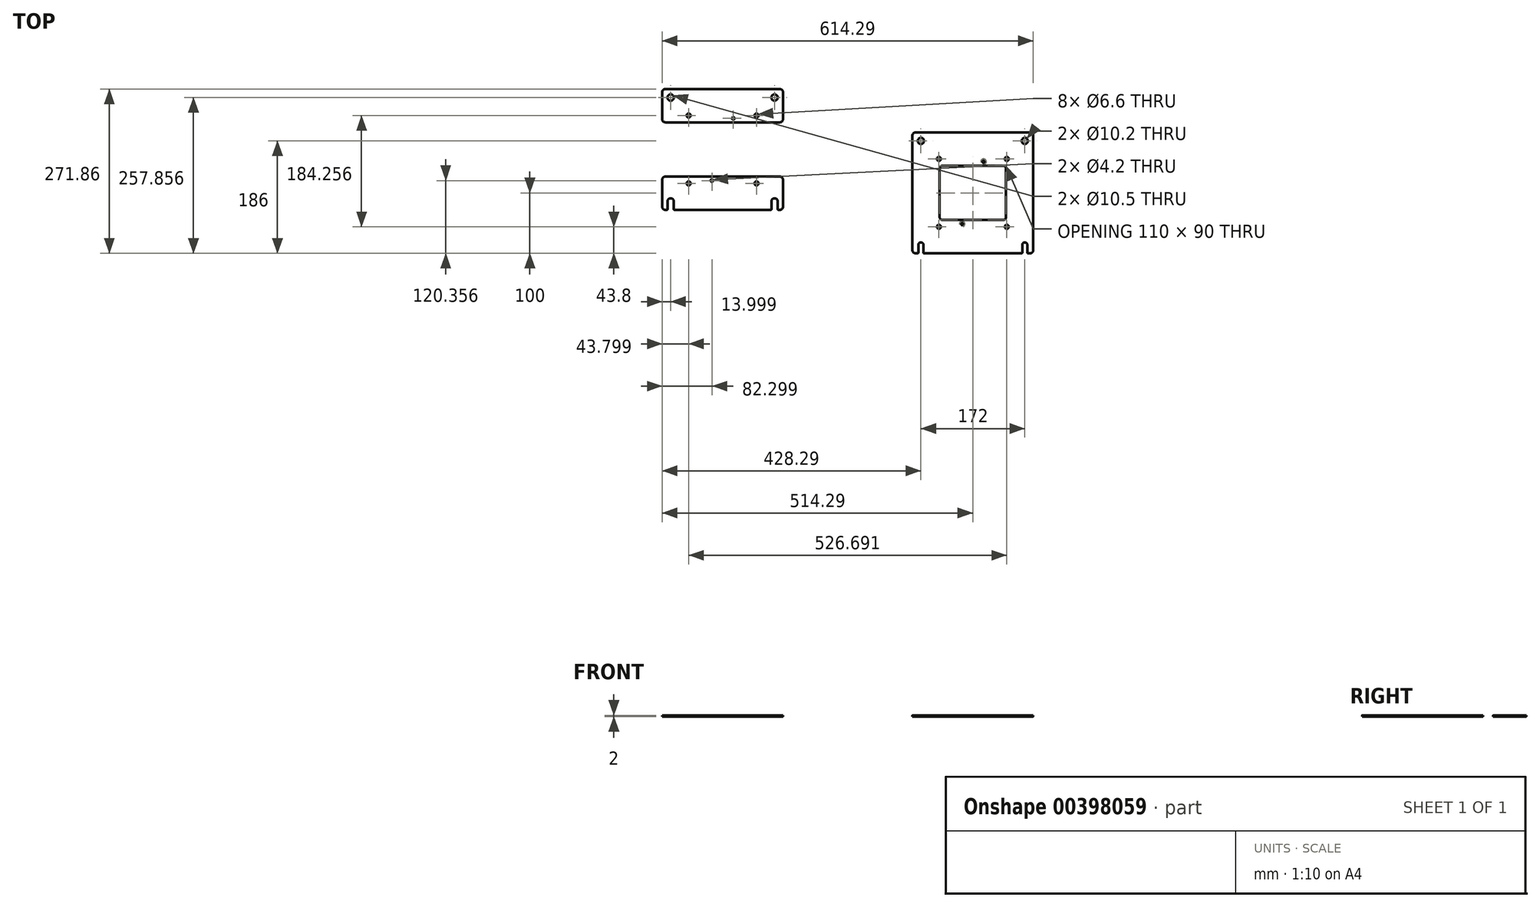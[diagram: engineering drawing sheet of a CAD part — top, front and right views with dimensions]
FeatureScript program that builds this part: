
annotation { "Feature Type Name" : "Feature", "Feature Type Description" : "" }
export const myFeature = defineFeature(function(context is Context, id is Id, definition is map)
    precondition{}
    {
        {
            var Q0;
            Q0=qCreatedBy(makeId("Top.planeOp"),FACE);
            var sketch = newSketch(context, id + "F0", { "sketchPlane" : qUnion([Q0])});
            skLineSegment(sketch, "E0.bottom", {"start": v(-95, -100) * mm, "end": v(-91.1, -100) * mm});
            skLineSegment(sketch, "E0.top", {"start": v(-95, 100) * mm, "end": v(95, 100) * mm});
            skLineSegment(sketch, "E0.left", {"start": v(-100, -95) * mm, "end": v(-100, 95) * mm});
            skLineSegment(sketch, "E0.right", {"start": v(100, -95) * mm, "end": v(100, 95) * mm});
            skPoint(sketch, "E0.middle", {"position": v(0, 0) * mm});
            skLineSegment(sketch, "E1.bottom", {"start": v(-50, -45) * mm, "end": v(50, -45) * mm});
            skLineSegment(sketch, "E1.top", {"start": v(-50, 45) * mm, "end": v(50, 45) * mm});
            skLineSegment(sketch, "E1.left", {"start": v(-55, -40) * mm, "end": v(-55, 40) * mm});
            skLineSegment(sketch, "E1.right", {"start": v(55, -40) * mm, "end": v(55, 40) * mm});
            skLineSegment(sketch, "E2", {"start": v(0, 119.48) * mm, "end": v(0, -138.55) * mm, "construction": true});
            skPoint(sketch, "E2.endSnap0", {"position": v(0, -45) * mm});
            skLineSegment(sketch, "E3", {"start": v(138.1, 0) * mm, "end": v(-145.7, 0) * mm, "construction": true});
            skPoint(sketch, "E4.visualSharp", {"position": v(-100, 100) * mm});
            skArc(sketch, "E4.filletArc", {"start": v(-95, 100) * mm, "mid": v(-98.54, 98.54) * mm, "end": v(-100, 95) * mm});
            skPoint(sketch, "E5.visualSharp", {"position": v(-100, -100) * mm});
            skArc(sketch, "E5.filletArc", {"start": v(-100, -95) * mm, "mid": v(-98.54, -98.54) * mm, "end": v(-95, -100) * mm});
            skPoint(sketch, "E6.visualSharp", {"position": v(100, -100) * mm});
            skArc(sketch, "E6.filletArc", {"start": v(95, -100) * mm, "mid": v(98.54, -98.54) * mm, "end": v(100, -95) * mm});
            skPoint(sketch, "E7.visualSharp", {"position": v(100, 100) * mm});
            skArc(sketch, "E7.filletArc", {"start": v(100, 95) * mm, "mid": v(98.54, 98.54) * mm, "end": v(95, 100) * mm});
            skPoint(sketch, "E8.visualSharp", {"position": v(-55, 45) * mm});
            skArc(sketch, "E8.filletArc", {"start": v(-50, 45) * mm, "mid": v(-53.54, 43.54) * mm, "end": v(-55, 40) * mm});
            skPoint(sketch, "E9.visualSharp", {"position": v(55, 45) * mm});
            skArc(sketch, "E9.filletArc", {"start": v(55, 40) * mm, "mid": v(53.54, 43.54) * mm, "end": v(50, 45) * mm});
            skPoint(sketch, "E10.visualSharp", {"position": v(55, -45) * mm});
            skArc(sketch, "E10.filletArc", {"start": v(50, -45) * mm, "mid": v(53.54, -43.54) * mm, "end": v(55, -40) * mm});
            skPoint(sketch, "E11.visualSharp", {"position": v(-55, -45) * mm});
            skArc(sketch, "E11.filletArc", {"start": v(-55, -40) * mm, "mid": v(-53.54, -43.54) * mm, "end": v(-50, -45) * mm});
            skCircle(sketch, "E12", {"center": v(-86, 86) * mm, "radius": 4.1 * mm});
            skCircle(sketch, "E13.MirrorC", {"center": v(86, 86) * mm, "radius": 4.1 * mm});
            skArc(sketch, "E14.MirrorC", {"start": v(-90.1, -86) * mm, "mid": v(-86, -81.9) * mm, "end": v(-81.9, -86) * mm});
            skArc(sketch, "E15.MirrorC", {"start": v(90.1, -86) * mm, "mid": v(86, -81.9) * mm, "end": v(81.9, -86) * mm});
            skPoint(sketch, "E16.centerSnap0", {"position": v(-53.54, 43.54) * mm});
            skCircle(sketch, "E17", {"center": v(-56.2, 56.2) * mm, "radius": 3.3 * mm});
            skCircle(sketch, "E18.MirrorC", {"center": v(56.2, 56.2) * mm, "radius": 3.3 * mm});
            skCircle(sketch, "E19.MirrorC", {"center": v(56.2, -56.2) * mm, "radius": 3.3 * mm});
            skCircle(sketch, "E20.MirrorC", {"center": v(-56.2, -56.2) * mm, "radius": 3.3 * mm});
            skCircle(sketch, "E21", {"center": v(17.7, 51.5) * mm, "radius": 1.55 * mm});
            skCircle(sketch, "E22", {"center": v(-17.7, -51.5) * mm, "radius": 1.55 * mm});
            skLineSegment(sketch, "E23", {"start": v(-81.9, -86) * mm, "end": v(-81.9, -99) * mm});
            skLineSegment(sketch, "E24", {"start": v(-90.1, -86) * mm, "end": v(-90.1, -99) * mm});
            skLineSegment(sketch, "E25.trimOffspring", {"start": v(-80.9, -100) * mm, "end": v(80.9, -100) * mm});
            skLineSegment(sketch, "E26.MirrorCS", {"start": v(81.9, -86) * mm, "end": v(81.9, -99) * mm});
            skLineSegment(sketch, "E27.MirrorCS", {"start": v(90.1, -86) * mm, "end": v(90.1, -99) * mm});
            skLineSegment(sketch, "E28.trimOffspring", {"start": v(91.1, -100) * mm, "end": v(95, -100) * mm});
            skPoint(sketch, "E29.visualSharp", {"position": v(-90.1, -100) * mm});
            skArc(sketch, "E29.filletArc", {"start": v(-91.1, -100) * mm, "mid": v(-90.4, -99.7) * mm, "end": v(-90.1, -99) * mm});
            skPoint(sketch, "E30.visualSharp", {"position": v(-81.9, -100) * mm});
            skArc(sketch, "E30.filletArc", {"start": v(-81.9, -99) * mm, "mid": v(-81.6, -99.7) * mm, "end": v(-80.9, -100) * mm});
            skPoint(sketch, "E31.visualSharp", {"position": v(90.1, -100) * mm});
            skArc(sketch, "E31.filletArc", {"start": v(90.1, -99) * mm, "mid": v(90.4, -99.7) * mm, "end": v(91.1, -100) * mm});
            skPoint(sketch, "E32.visualSharp", {"position": v(81.9, -100) * mm});
            skArc(sketch, "E32.filletArc", {"start": v(80.9, -100) * mm, "mid": v(81.6, -99.7) * mm, "end": v(81.9, -99) * mm});
            skLineSegment(sketch, "E33.bottom", {"start": v(-509.3, -28.14) * mm, "end": v(-506.54, -28.14) * mm});
            skLineSegment(sketch, "E33.top", {"start": v(-509.3, 171.86) * mm, "end": v(-319.3, 171.86) * mm});
            skLineSegment(sketch, "E33.left", {"start": v(-514.3, -23.14) * mm, "end": v(-514.3, 21.86) * mm});
            skLineSegment(sketch, "E33.right", {"start": v(-314.3, -23.14) * mm, "end": v(-314.3, 21.86) * mm});
            skPoint(sketch, "E33.middle", {"position": v(-414.3, 71.86) * mm});
            skLineSegment(sketch, "E34.bottom", {"start": v(-464.3, 26.86) * mm, "end": v(-364.3, 26.86) * mm});
            skLineSegment(sketch, "E34.top", {"start": v(-464.3, 116.86) * mm, "end": v(-364.3, 116.86) * mm});
            skLineSegment(sketch, "E35", {"start": v(-414.3, 191.33) * mm, "end": v(-414.3, -66.7) * mm, "construction": true});
            skPoint(sketch, "E35.endSnap0", {"position": v(-414.3, 26.86) * mm});
            skLineSegment(sketch, "E36", {"start": v(-276.2, 71.86) * mm, "end": v(-560, 71.86) * mm, "construction": true});
            skPoint(sketch, "E37.visualSharp", {"position": v(-514.3, 171.86) * mm});
            skArc(sketch, "E37.filletArc", {"start": v(-509.3, 171.86) * mm, "mid": v(-512.83, 170.4) * mm, "end": v(-514.3, 166.86) * mm});
            skPoint(sketch, "E38.visualSharp", {"position": v(-514.3, -28.14) * mm});
            skArc(sketch, "E38.filletArc", {"start": v(-514.3, -23.14) * mm, "mid": v(-512.83, -26.68) * mm, "end": v(-509.3, -28.14) * mm});
            skPoint(sketch, "E39.visualSharp", {"position": v(-314.3, -28.14) * mm});
            skArc(sketch, "E39.filletArc", {"start": v(-319.3, -28.14) * mm, "mid": v(-315.76, -26.68) * mm, "end": v(-314.3, -23.14) * mm});
            skPoint(sketch, "E40.visualSharp", {"position": v(-314.3, 171.86) * mm});
            skArc(sketch, "E40.filletArc", {"start": v(-314.3, 166.86) * mm, "mid": v(-315.76, 170.4) * mm, "end": v(-319.3, 171.86) * mm});
            skPoint(sketch, "E41.visualSharp", {"position": v(-359.3, 116.86) * mm});
            skPoint(sketch, "E42.visualSharp", {"position": v(-359.3, 26.86) * mm});
            skPoint(sketch, "E43.visualSharp", {"position": v(-469.3, 26.86) * mm});
            skCircle(sketch, "E44", {"center": v(-500.3, 157.86) * mm, "radius": 5.25 * mm});
            skCircle(sketch, "E45.MirrorC", {"center": v(-328.3, 157.86) * mm, "radius": 5.25 * mm});
            skArc(sketch, "E46.MirrorC", {"start": v(-505.54, -14.14) * mm, "mid": v(-500.3, -8.9) * mm, "end": v(-495.04, -14.14) * mm});
            skArc(sketch, "E47.MirrorC", {"start": v(-323.04, -14.14) * mm, "mid": v(-328.3, -8.9) * mm, "end": v(-333.54, -14.14) * mm});
            skCircle(sketch, "E48", {"center": v(-470.5, 128.06) * mm, "radius": 3.3 * mm});
            skCircle(sketch, "E49.MirrorC", {"center": v(-358.1, 128.06) * mm, "radius": 3.3 * mm});
            skCircle(sketch, "E50.MirrorC", {"center": v(-358.1, 15.66) * mm, "radius": 3.3 * mm});
            skCircle(sketch, "E51.MirrorC", {"center": v(-470.5, 15.66) * mm, "radius": 3.3 * mm});
            skCircle(sketch, "E52", {"center": v(-396.6, 123.36) * mm, "radius": 2.1 * mm});
            skCircle(sketch, "E53", {"center": v(-432, 20.36) * mm, "radius": 2.1 * mm});
            skLineSegment(sketch, "E54", {"start": v(-495.04, -14.14) * mm, "end": v(-495.04, -27.14) * mm});
            skLineSegment(sketch, "E55", {"start": v(-505.54, -14.14) * mm, "end": v(-505.54, -27.14) * mm});
            skLineSegment(sketch, "E56.trimOffspring", {"start": v(-494.04, -28.14) * mm, "end": v(-334.54, -28.14) * mm});
            skLineSegment(sketch, "E57.MirrorCS", {"start": v(-333.54, -14.14) * mm, "end": v(-333.54, -27.14) * mm});
            skLineSegment(sketch, "E58.MirrorCS", {"start": v(-323.04, -14.14) * mm, "end": v(-323.04, -27.14) * mm});
            skLineSegment(sketch, "E59.trimOffspring", {"start": v(-322.04, -28.14) * mm, "end": v(-319.3, -28.14) * mm});
            skPoint(sketch, "E60.visualSharp", {"position": v(-505.54, -28.14) * mm});
            skArc(sketch, "E60.filletArc", {"start": v(-506.54, -28.14) * mm, "mid": v(-505.83, -27.85) * mm, "end": v(-505.54, -27.14) * mm});
            skPoint(sketch, "E61.visualSharp", {"position": v(-495.04, -28.14) * mm});
            skArc(sketch, "E61.filletArc", {"start": v(-495.04, -27.14) * mm, "mid": v(-494.75, -27.85) * mm, "end": v(-494.04, -28.14) * mm});
            skPoint(sketch, "E62.visualSharp", {"position": v(-323.04, -28.14) * mm});
            skArc(sketch, "E62.filletArc", {"start": v(-323.04, -27.14) * mm, "mid": v(-322.75, -27.85) * mm, "end": v(-322.04, -28.14) * mm});
            skPoint(sketch, "E63.visualSharp", {"position": v(-333.54, -28.14) * mm});
            skArc(sketch, "E63.filletArc", {"start": v(-334.54, -28.14) * mm, "mid": v(-333.83, -27.85) * mm, "end": v(-333.54, -27.14) * mm});
            skLineSegment(sketch, "E64", {"start": v(-364.3, 116.86) * mm, "end": v(-319.3, 116.86) * mm});
            skLineSegment(sketch, "E65", {"start": v(-464.3, 116.86) * mm, "end": v(-509.3, 116.86) * mm});
            skLineSegment(sketch, "E66", {"start": v(-364.3, 26.86) * mm, "end": v(-319.3, 26.86) * mm});
            skLineSegment(sketch, "E67", {"start": v(-464.3, 26.86) * mm, "end": v(-509.3, 26.86) * mm});
            skLineSegment(sketch, "E68.trimOffspring", {"start": v(-314.3, 121.86) * mm, "end": v(-314.3, 166.86) * mm});
            skLineSegment(sketch, "E69.trimOffspring", {"start": v(-514.3, 121.86) * mm, "end": v(-514.3, 166.86) * mm});
            skPoint(sketch, "E70.visualSharp", {"position": v(-514.3, 116.86) * mm});
            skArc(sketch, "E70.filletArc", {"start": v(-514.3, 121.86) * mm, "mid": v(-512.83, 118.32) * mm, "end": v(-509.3, 116.86) * mm});
            skPoint(sketch, "E71.visualSharp", {"position": v(-314.3, 116.86) * mm});
            skArc(sketch, "E71.filletArc", {"start": v(-319.3, 116.86) * mm, "mid": v(-315.76, 118.32) * mm, "end": v(-314.3, 121.86) * mm});
            skPoint(sketch, "E72.visualSharp", {"position": v(-514.3, 26.86) * mm});
            skArc(sketch, "E72.filletArc", {"start": v(-509.3, 26.86) * mm, "mid": v(-512.83, 25.4) * mm, "end": v(-514.3, 21.86) * mm});
            skPoint(sketch, "E73.visualSharp", {"position": v(-314.3, 26.86) * mm});
            skArc(sketch, "E73.filletArc", {"start": v(-314.3, 21.86) * mm, "mid": v(-315.76, 25.4) * mm, "end": v(-319.3, 26.86) * mm});
            skCircle(sketch, "E74", {"center": v(-86, 86) * mm, "radius": 5.1 * mm});
            skCircle(sketch, "E75", {"center": v(86, 86) * mm, "radius": 5.1 * mm});
            skSolve(sketch);
        }
        {
            var Q0;
            Q0 = qSketchRegion(id + "F0", true);
            extrude(context, id + "F1", {"entities" : qUnion([Q0]), "depth" : 2 * mm});
        }
        {
            var Q0;
            Q0=makeQuery(id+"F1.opExtrude","CAP_FACE",FACE,{"disambiguationData":[OSD([sQuery(id+"F0.wireOp",EDGE,"E0.bottom"),sQuery(id+"F0.wireOp",EDGE,"E0.top"),sQuery(id+"F0.wireOp",EDGE,"E0.left"),sQuery(id+"F0.wireOp",EDGE,"E0.right"),sQuery(id+"F0.wireOp",EDGE,"E1.bottom"),sQuery(id+"F0.wireOp",EDGE,"E1.top"),sQuery(id+"F0.wireOp",EDGE,"E1.left"),sQuery(id+"F0.wireOp",EDGE,"E1.right"),sQuery(id+"F0.wireOp",EDGE,"E4.filletArc"),sQuery(id+"F0.wireOp",EDGE,"E5.filletArc"),sQuery(id+"F0.wireOp",EDGE,"E6.filletArc"),sQuery(id+"F0.wireOp",EDGE,"E7.filletArc"),sQuery(id+"F0.wireOp",EDGE,"E8.filletArc"),sQuery(id+"F0.wireOp",EDGE,"E9.filletArc"),sQuery(id+"F0.wireOp",EDGE,"E10.filletArc"),sQuery(id+"F0.wireOp",EDGE,"E11.filletArc"),sQuery(id+"F0.wireOp",EDGE,"E12"),sQuery(id+"F0.wireOp",EDGE,"E13.MirrorC"),sQuery(id+"F0.wireOp",EDGE,"E14.MirrorC"),sQuery(id+"F0.wireOp",EDGE,"E15.MirrorC"),sQuery(id+"F0.wireOp",EDGE,"E17"),sQuery(id+"F0.wireOp",EDGE,"E18.MirrorC"),sQuery(id+"F0.wireOp",EDGE,"E19.MirrorC"),sQuery(id+"F0.wireOp",EDGE,"E20.MirrorC"),sQuery(id+"F0.wireOp",EDGE,"E21"),sQuery(id+"F0.wireOp",EDGE,"E22"),sQuery(id+"F0.wireOp",EDGE,"E23"),sQuery(id+"F0.wireOp",EDGE,"E24"),sQuery(id+"F0.wireOp",EDGE,"E25.trimOffspring"),sQuery(id+"F0.wireOp",EDGE,"E26.MirrorCS"),sQuery(id+"F0.wireOp",EDGE,"E27.MirrorCS"),sQuery(id+"F0.wireOp",EDGE,"E28.trimOffspring"),sQuery(id+"F0.wireOp",EDGE,"E29.filletArc"),sQuery(id+"F0.wireOp",EDGE,"E30.filletArc"),sQuery(id+"F0.wireOp",EDGE,"E31.filletArc"),sQuery(id+"F0.wireOp",EDGE,"E32.filletArc")])],"isStart":true});
            var sketch = newSketch(context, id + "F2", { "sketchPlane" : qUnion([Q0])});
            skCircle(sketch, "E76", {"center": v(17.7, -51.5) * mm, "radius": 2.8 * mm});
            skCircle(sketch, "E77", {"center": v(-17.7, 51.5) * mm, "radius": 2.8 * mm});
            skSolve(sketch);
        }
        {
            var Q0;
            Q0 = qSketchRegion(id + "F2", true);
            extrude(context, id + "F3", {"entities" : qUnion([Q0]), "operationType" : NewBodyOperationType.REMOVE, "oppositeDirection" : true, "depth" : 1.65 * mm, "hasDraft" : true, "draftAngle" : 46 * degree});
        }
    });
